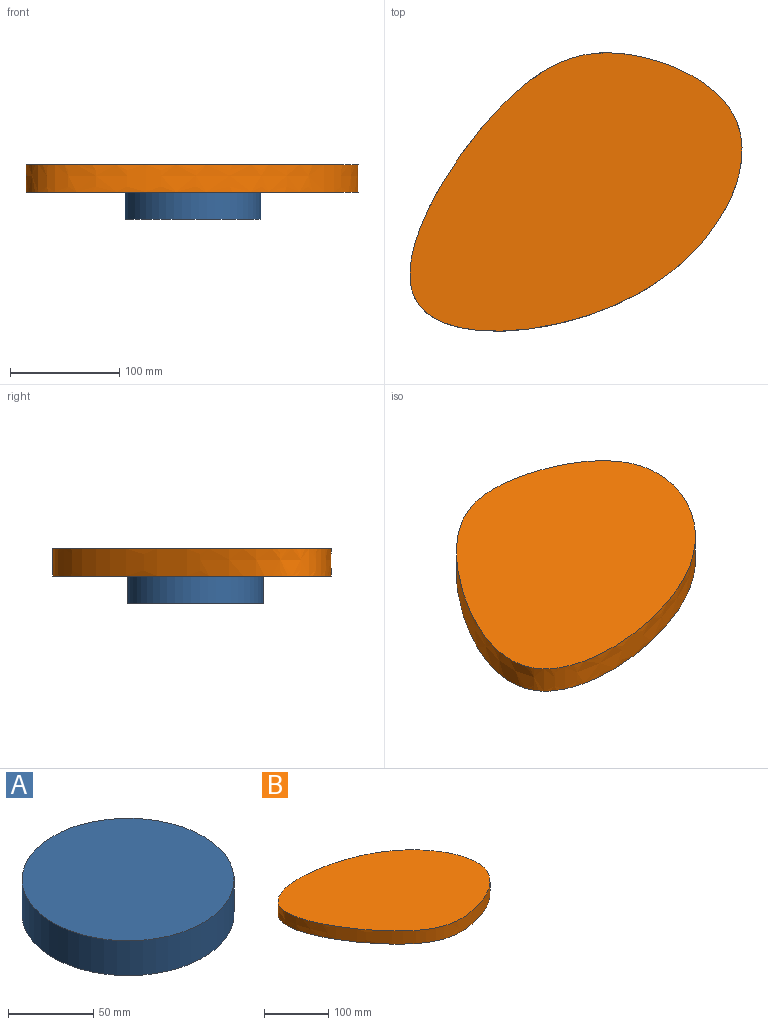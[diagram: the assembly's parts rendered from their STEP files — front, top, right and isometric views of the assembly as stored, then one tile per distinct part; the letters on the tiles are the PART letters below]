
ASSEMBLY  parts=2 mates=1
PART A: 3 faces, bbox 124.3x124.3x25 mm
  f0: cylinder r=62.14mm len=124.28mm, axis (0,0,-1), area 9760.8mm2, adj f1,f2
  f1: plane 124.28x124.28mm, normal (0,0,1), area 12130.7mm2, adj f0
  f2: plane 124.28x124.28mm, normal (0,0,-1), area 12130.7mm2, adj f0
PART B: 3 faces, bbox 324.5x275x25 mm
  f0: extruded ~303.67x253.98mm, area 21722.7mm2, adj f1,f2
  f1: plane 324.45x274.97mm, normal (0,0,1), area 55143.8mm2, adj f0
  f2: plane 324.45x274.97mm, normal (0,0,-1), area 55143.8mm2, adj f0
PLACE A t=(-33.03,17.81,-12.2)mm
PLACE B rot(axis=(1,0,0),180deg) t=(-50.37,44.48,37.8)mm
MATE cylindrical B.f1 <-> A.f0  axis (0,0,-1) through (-33.03,17.81,12.8)mm
